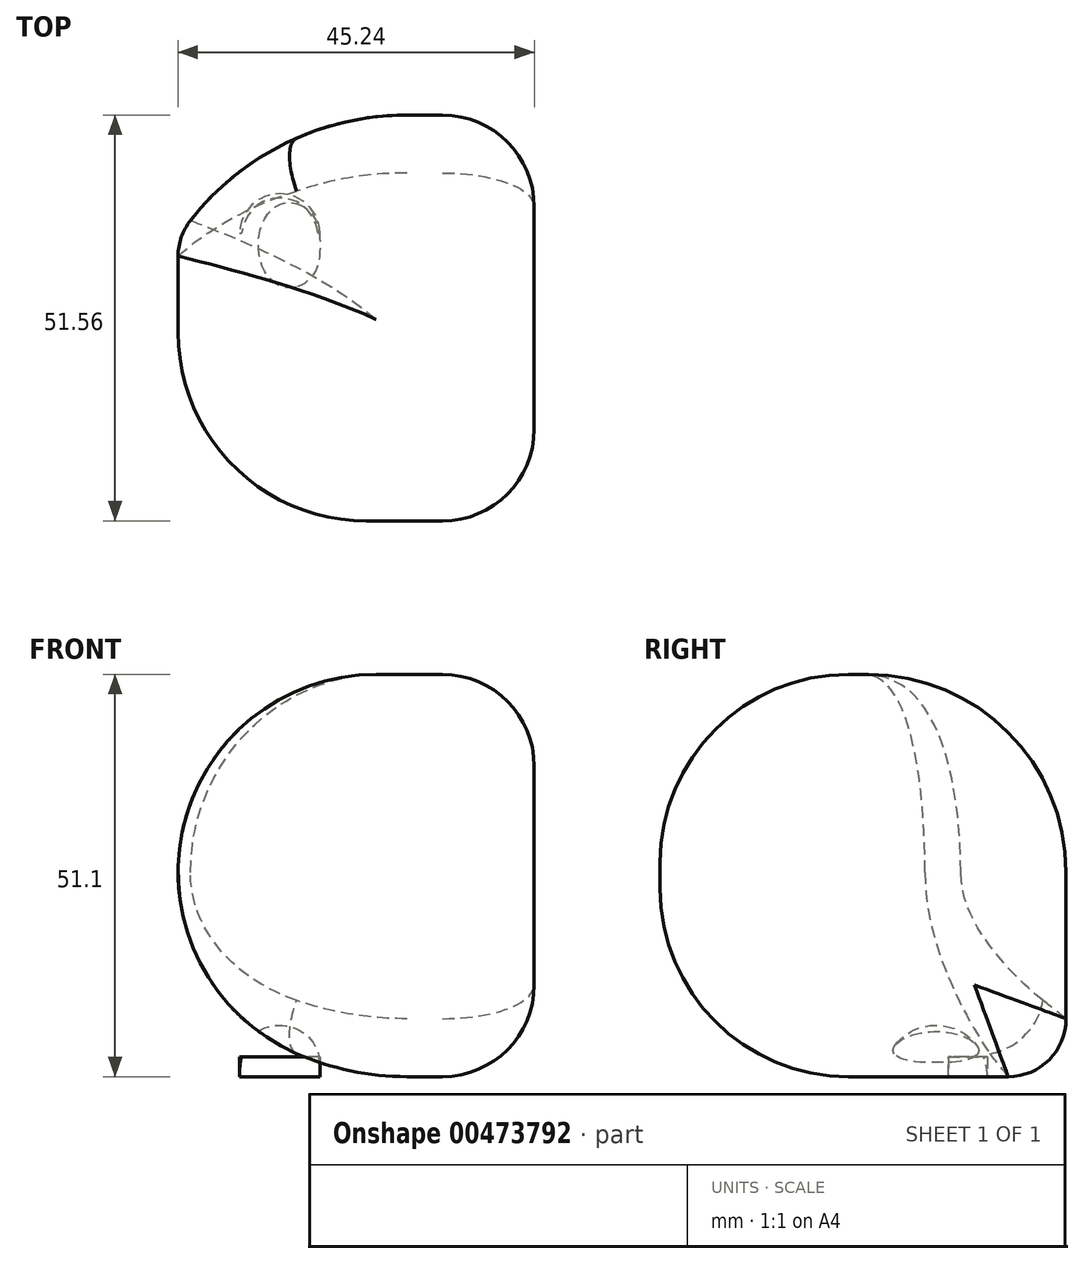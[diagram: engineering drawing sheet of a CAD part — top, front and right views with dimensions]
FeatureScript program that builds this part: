
annotation { "Feature Type Name" : "Feature", "Feature Type Description" : "" }
export const myFeature = defineFeature(function(context is Context, id is Id, definition is map)
    precondition{}
    {
        {
            var Q0;
            Q0=qCreatedBy(makeId("Top.planeOp"),FACE);
            var sketch = newSketch(context, id + "F0", { "sketchPlane" : qUnion([Q0])});
            skLineSegment(sketch, "E0.bottom", {"start": v(25.56, 25.78) * mm, "end": v(-25.56, 25.78) * mm});
            skLineSegment(sketch, "E0.top", {"start": v(25.56, -25.78) * mm, "end": v(-25.56, -25.78) * mm});
            skLineSegment(sketch, "E0.left", {"start": v(25.56, 25.78) * mm, "end": v(25.56, -25.78) * mm});
            skLineSegment(sketch, "E0.right", {"start": v(-25.56, 25.78) * mm, "end": v(-25.56, -25.78) * mm});
            skPoint(sketch, "E0.middle", {"position": v(0, 0) * mm});
            skSolve(sketch);
        }
        {
            var Q0;
            Q0=makeQuery(id+"F0.imprint","IMPRINT",FACE,{"disambiguationData":[TD([[makeQuery(id+"F0.imprint","IMPRINT",EDGE,{"derivedFrom":sQuery(id+"F0.wireOp",EDGE,"E0.bottom")}),1.0]])]});
            extrude(context, id + "F1", {"entities" : qUnion([Q0]), "depth" : 51.1 * mm});
        }
        {
            var Q0;
            Q0=makeQuery(id+"F1.opExtrude","CAP_EDGE",EDGE,{"disambiguationData":[OSD([sQuery(id+"F0.wireOp",EDGE,"E0.bottom")])],"isStart":true});
            fillet(context, id + "F2", {"entities" : qUnion([Q0]), "radius" : 7.36 * mm, "tangentPropagation" : true, "allowEdgeOverflow" : false});
        }
        {
            var Q0;
            Q0=makeQuery(id+"F1.opExtrude","SWEPT_EDGE",EDGE,{"disambiguationData":[OSD([sQuery(id+"F0.wireOp",EDGE,"E0.bottom"),sQuery(id+"F0.wireOp",EDGE,"E0.right")])]});
            fillet(context, id + "F3", {"entities" : qUnion([Q0]), "radius" : 34.95 * mm, "tangentPropagation" : true, "allowEdgeOverflow" : false});
        }
        {
            var Q0;
            {var subQ0=sQuery(id+"F0.wireOp",EDGE,"E0.right");var subQ1=sQuery(id+"F0.wireOp",EDGE,"E0.bottom");Q0=makeQuery(id+"F3.opFillet","BLEND_EDGE",EDGE,{"blendedFrom":[makeQuery(id+"F1.opExtrude","SWEPT_EDGE",EDGE,{"disambiguationData":[OSD([subQ1,subQ0])]}),makeQuery(id+"F1.opExtrude","CAP_FACE",FACE,{"disambiguationData":[OSD([subQ1,sQuery(id+"F0.wireOp",EDGE,"E0.top"),sQuery(id+"F0.wireOp",EDGE,"E0.left"),subQ0])],"isStart":false})],"blendedInto":[makeQuery(id+"F1.opExtrude","CAP_FACE",FACE,{"disambiguationData":[OSD([subQ1,sQuery(id+"F0.wireOp",EDGE,"E0.top"),sQuery(id+"F0.wireOp",EDGE,"E0.left"),subQ0])],"isStart":false})]});}
            fillet(context, id + "F4", {"entities" : qUnion([Q0]), "radius" : 25.14 * mm, "tangentPropagation" : true, "allowEdgeOverflow" : false});
        }
        {
            var Q0;
            Q0=makeQuery(id+"F4.opFillet","BLEND_EDGE",EDGE,{"blendedFrom":[makeQuery(id+"F1.opExtrude","CAP_EDGE",EDGE,{"disambiguationData":[OSD([sQuery(id+"F0.wireOp",EDGE,"E0.right")])],"isStart":false}),makeQuery(id+"F1.opExtrude","SWEPT_FACE",FACE,{"disambiguationData":[OSD([sQuery(id+"F0.wireOp",EDGE,"E0.top")])]})],"blendedInto":[makeQuery(id+"F1.opExtrude","SWEPT_FACE",FACE,{"disambiguationData":[OSD([sQuery(id+"F0.wireOp",EDGE,"E0.top")])]})]});
            fillet(context, id + "F5", {"entities" : qUnion([Q0]), "radius" : 23.92 * mm, "tangentPropagation" : true, "allowEdgeOverflow" : false});
        }
        {
            var Q0;
            Q0=makeQuery(id+"F2.opFillet","BLEND_EDGE",EDGE,{"blendedFrom":[makeQuery(id+"F1.opExtrude","CAP_EDGE",EDGE,{"disambiguationData":[OSD([sQuery(id+"F0.wireOp",EDGE,"E0.bottom")])],"isStart":true}),makeQuery(id+"F1.opExtrude","SWEPT_FACE",FACE,{"disambiguationData":[OSD([sQuery(id+"F0.wireOp",EDGE,"E0.left")])]})],"blendedInto":[makeQuery(id+"F1.opExtrude","SWEPT_FACE",FACE,{"disambiguationData":[OSD([sQuery(id+"F0.wireOp",EDGE,"E0.left")])]})]});
            fillet(context, id + "F6", {"entities" : qUnion([Q0]), "radius" : 11.65 * mm, "tangentPropagation" : true, "allowEdgeOverflow" : false});
        }
        {
            var Q0;
            Q0=qCreatedBy(makeId("Top.planeOp"),FACE);
            var sketch = newSketch(context, id + "F7", { "sketchPlane" : qUnion([Q0])});
            skArc(sketch, "E1", {"start": v(-1.65, 10.81) * mm, "mid": v(-6.76, 15.78) * mm, "end": v(-11.87, 10.81) * mm});
            skLineSegment(sketch, "E2", {"start": v(-11.87, 10.81) * mm, "end": v(-1.65, 10.81) * mm});
            skSolve(sketch);
        }
        {
            var Q0;
            Q0=makeQuery(id+"F7.imprint","IMPRINT",FACE,{"disambiguationData":[TD([[makeQuery(id+"F7.imprint","IMPRINT",EDGE,{"derivedFrom":sQuery(id+"F7.wireOp",EDGE,"E1")}),1.0]])]});
            extrude(context, id + "F8", {"entities" : qUnion([Q0]), "depth" : 2.54 * mm});
        }
        {
            var Q0;
            Q0=qCreatedBy(makeId("Top.planeOp"),FACE);
            var sketch = newSketch(context, id + "F9", { "sketchPlane" : qUnion([Q0])});
            skLineSegment(sketch, "E3", {"start": v(-21.72, 9.24) * mm, "end": v(18.44, 9.24) * mm});
            skSolve(sketch);
        }
        {
            var Q0;
            Q0=makeQuery(id+"F8.opExtrude","CAP_FACE",FACE,{"disambiguationData":[OSD([sQuery(id+"F7.wireOp",EDGE,"E1"),sQuery(id+"F7.wireOp",EDGE,"E2")])],"isStart":true});
            var Q1;
            Q1=sQuery(id+"F9.wireOp",EDGE,"E3");
            revolve(context, id + "F10", {"operationType" : NewBodyOperationType.REMOVE, "entities" : qUnion([Q0]), "axis" : qUnion([Q1]), "revolveType" : RevolveType.FULL, "oppositeDirection" : true});
        }
    });
